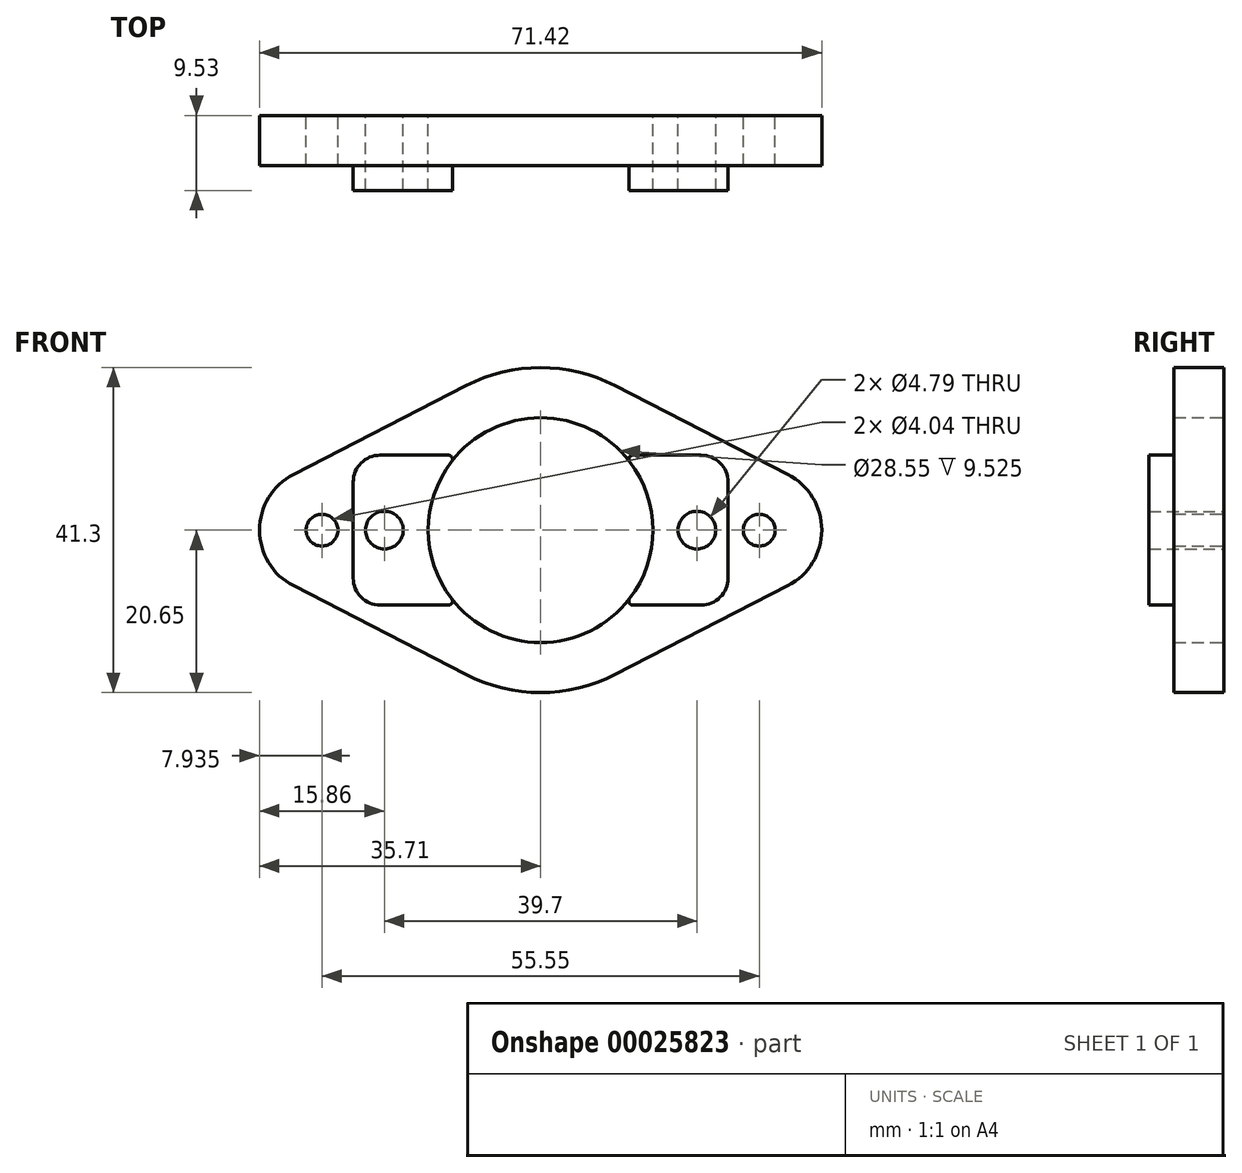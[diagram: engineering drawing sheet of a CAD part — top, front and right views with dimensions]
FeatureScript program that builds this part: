
annotation { "Feature Type Name" : "Feature", "Feature Type Description" : "" }
export const myFeature = defineFeature(function(context is Context, id is Id, definition is map)
    precondition{}
    {
        {
            var Q0;
            Q0=qCreatedBy(makeId("Front.planeOp"),FACE);
            var sketch = newSketch(context, id + "F0", { "sketchPlane" : qUnion([Q0])});
            skArc(sketch, "E0", {"start": v(-9.45, -18.36) * mm, "mid": v(0, -20.65) * mm, "end": v(9.45, -18.36) * mm});
            skArc(sketch, "E1", {"start": v(-31.4, 7.06) * mm, "mid": v(-35.71, 0) * mm, "end": v(-31.4, -7.06) * mm});
            skArc(sketch, "E2", {"start": v(31.4, -7.06) * mm, "mid": v(35.71, 0) * mm, "end": v(31.4, 7.06) * mm});
            skLineSegment(sketch, "E3", {"start": v(0, 32.22) * mm, "end": v(0, 0) * mm, "construction": true});
            skLineSegment(sketch, "E4", {"start": v(0, 0) * mm, "end": v(27.77, 0) * mm, "construction": true});
            skLineSegment(sketch, "E5", {"start": v(-31.4, 7.06) * mm, "end": v(-9.45, 18.36) * mm});
            skLineSegment(sketch, "E6", {"start": v(9.45, 18.36) * mm, "end": v(31.4, 7.06) * mm});
            skLineSegment(sketch, "E7", {"start": v(31.4, -7.06) * mm, "end": v(9.45, -18.36) * mm});
            skLineSegment(sketch, "E8", {"start": v(-31.4, -7.06) * mm, "end": v(-9.45, -18.36) * mm});
            skArc(sketch, "E9.trimOffspring", {"start": v(9.45, 18.36) * mm, "mid": v(0, 20.65) * mm, "end": v(-9.45, 18.36) * mm});
            skCircle(sketch, "E10", {"center": v(0, 0) * mm, "radius": 14.27 * mm});
            skSolve(sketch);
        }
        {
            var Q0;
            Q0=makeQuery(id+"F0.imprint","IMPRINT",FACE,{"disambiguationData":[TD([[makeQuery(id+"F0.imprint","IMPRINT",EDGE,{"derivedFrom":sQuery(id+"F0.wireOp",EDGE,"E0")}),1.0]])]});
            extrude(context, id + "F1", {"entities" : qUnion([Q0]), "depth" : 6.35 * mm});
        }
        {
            var Q0;
            Q0=makeQuery(id+"F1.opExtrude","CAP_FACE",FACE,{"disambiguationData":[OSD([sQuery(id+"F0.wireOp",EDGE,"E0"),sQuery(id+"F0.wireOp",EDGE,"E1"),sQuery(id+"F0.wireOp",EDGE,"E2"),sQuery(id+"F0.wireOp",EDGE,"E5"),sQuery(id+"F0.wireOp",EDGE,"E6"),sQuery(id+"F0.wireOp",EDGE,"E7"),sQuery(id+"F0.wireOp",EDGE,"E8"),sQuery(id+"F0.wireOp",EDGE,"E9.trimOffspring"),sQuery(id+"F0.wireOp",EDGE,"E10")])],"isStart":false});
            var sketch = newSketch(context, id + "F2", { "sketchPlane" : qUnion([Q0])});
            skLineSegment(sketch, "E11.rect.bottom", {"start": v(20.38, 9.53) * mm, "end": v(-20.38, 9.53) * mm});
            skLineSegment(sketch, "E11.rect.top", {"start": v(20.38, -9.53) * mm, "end": v(-20.38, -9.53) * mm});
            skLineSegment(sketch, "E11.rect.left", {"start": v(23.81, 6.1) * mm, "end": v(23.81, -6.1) * mm});
            skLineSegment(sketch, "E11.rect.right", {"start": v(-23.81, 6.1) * mm, "end": v(-23.81, -6.1) * mm});
            skPoint(sketch, "E11.rect.middle", {"position": v(0, 0) * mm});
            skPoint(sketch, "E12.visualSharp", {"position": v(23.81, 9.53) * mm});
            skArc(sketch, "E12.filletArc", {"start": v(23.81, 6.1) * mm, "mid": v(22.8, 8.52) * mm, "end": v(20.38, 9.53) * mm});
            skPoint(sketch, "E13.visualSharp", {"position": v(23.81, -9.53) * mm});
            skArc(sketch, "E13.filletArc", {"start": v(20.38, -9.53) * mm, "mid": v(22.8, -8.52) * mm, "end": v(23.81, -6.1) * mm});
            skPoint(sketch, "E14.visualSharp", {"position": v(-23.81, 9.53) * mm});
            skArc(sketch, "E14.filletArc", {"start": v(-20.38, 9.53) * mm, "mid": v(-22.8, 8.52) * mm, "end": v(-23.81, 6.1) * mm});
            skPoint(sketch, "E15.visualSharp", {"position": v(-23.81, -9.53) * mm});
            skArc(sketch, "E15.filletArc", {"start": v(-23.81, -6.1) * mm, "mid": v(-22.8, -8.52) * mm, "end": v(-20.38, -9.53) * mm});
            skCircle(sketch, "E16.0", {"center": v(0, 0) * mm, "radius": 14.27 * mm});
            skSolve(sketch);
        }
        {
            var Q0;
            Q0=makeQuery(id+"F2.imprint","IMPRINT",FACE,{"disambiguationData":[TD([[makeQuery(id+"F2.imprint","IMPRINT",EDGE,{"derivedFrom":sQuery(id+"F2.wireOp",EDGE,"E11.rect.right")}),1.0]])]});
            var Q1;
            Q1=makeQuery(id+"F2.imprint","IMPRINT",FACE,{"disambiguationData":[TD([[makeQuery(id+"F2.imprint","IMPRINT",EDGE,{"derivedFrom":sQuery(id+"F2.wireOp",EDGE,"E11.rect.left")}),-1.0]])]});
            extrude(context, id + "F3", {"entities" : qUnion([Q0, Q1]), "operationType" : NewBodyOperationType.ADD, "depth" : 3.17 * mm});
        }
        {
            var Q0;
            {var subQ0=sQuery(id+"F2.wireOp",EDGE,"E11.rect.bottom");var subQ1=sQuery(id+"F2.wireOp",EDGE,"E16.0");Q0=makeQuery(id+"F3.opExtrude","SWEPT_EDGE",EDGE,{"disambiguationData":[OSD([subQ0,subQ1]),TDD([makeQuery(id+"F2.imprint","INTERSECT",VERTEX,{"disambiguationData":[OD(1.0)],"derivedFrom":[subQ0,subQ1]})])]});}
            var Q1;
            {var subQ0=sQuery(id+"F2.wireOp",EDGE,"E11.rect.top");var subQ1=sQuery(id+"F2.wireOp",EDGE,"E16.0");Q1=makeQuery(id+"F3.opExtrude","SWEPT_EDGE",EDGE,{"disambiguationData":[OSD([subQ0,subQ1]),TDD([makeQuery(id+"F2.imprint","INTERSECT",VERTEX,{"disambiguationData":[OD(1.0)],"derivedFrom":[subQ0,subQ1]})])]});}
            var Q2;
            {var subQ0=sQuery(id+"F2.wireOp",EDGE,"E11.rect.bottom");var subQ1=sQuery(id+"F2.wireOp",EDGE,"E16.0");Q2=makeQuery(id+"F3.opExtrude","SWEPT_EDGE",EDGE,{"disambiguationData":[OSD([subQ0,subQ1]),TDD([makeQuery(id+"F2.imprint","INTERSECT",VERTEX,{"disambiguationData":[OD(0.0)],"derivedFrom":[subQ0,subQ1]})])]});}
            var Q3;
            {var subQ0=sQuery(id+"F2.wireOp",EDGE,"E11.rect.top");var subQ1=sQuery(id+"F2.wireOp",EDGE,"E16.0");Q3=makeQuery(id+"F3.opExtrude","SWEPT_EDGE",EDGE,{"disambiguationData":[OSD([subQ0,subQ1]),TDD([makeQuery(id+"F2.imprint","INTERSECT",VERTEX,{"disambiguationData":[OD(0.0)],"derivedFrom":[subQ0,subQ1]})])]});}
            fillet(context, id + "F4", {"entities" : qUnion([Q0, Q1, Q2, Q3]), "radius" : 0.5 * mm, "tangentPropagation" : true, "allowEdgeOverflow" : false});
        }
        {
            var Q0;
            Q0=makeQuery(id+"F1.opExtrude","CAP_FACE",FACE,{"disambiguationData":[OSD([sQuery(id+"F0.wireOp",EDGE,"E0"),sQuery(id+"F0.wireOp",EDGE,"E1"),sQuery(id+"F0.wireOp",EDGE,"E2"),sQuery(id+"F0.wireOp",EDGE,"E5"),sQuery(id+"F0.wireOp",EDGE,"E6"),sQuery(id+"F0.wireOp",EDGE,"E7"),sQuery(id+"F0.wireOp",EDGE,"E8"),sQuery(id+"F0.wireOp",EDGE,"E9.trimOffspring"),sQuery(id+"F0.wireOp",EDGE,"E10")])],"isStart":true});
            var sketch = newSketch(context, id + "F5", { "sketchPlane" : qUnion([Q0])});
            skLineSegment(sketch, "E17", {"start": v(-27.77, 0) * mm, "end": v(27.77, 0) * mm});
            skPoint(sketch, "E18", {"position": v(-19.85, 0) * mm});
            skPoint(sketch, "E19", {"position": v(19.85, 0) * mm});
            skLineSegment(sketch, "E20", {"start": v(0, 30.11) * mm, "end": v(0, 0) * mm, "construction": true});
            skSolve(sketch);
        }
        {
            var Q0;
            Q0=sQuery(id+"F5.wireOp",VERTEX,"E18");
            var Q1;
            Q1=sQuery(id+"F5.wireOp",VERTEX,"E19");
            var Q2;
            Q2=makeQuery(id+"F1.opExtrude","SWEPT_BODY",BODY,{"disambiguationData":[OSD([sQuery(id+"F0.wireOp",EDGE,"E0"),sQuery(id+"F0.wireOp",EDGE,"E1"),sQuery(id+"F0.wireOp",EDGE,"E2"),sQuery(id+"F0.wireOp",EDGE,"E5"),sQuery(id+"F0.wireOp",EDGE,"E6"),sQuery(id+"F0.wireOp",EDGE,"E7"),sQuery(id+"F0.wireOp",EDGE,"E8"),sQuery(id+"F0.wireOp",EDGE,"E9.trimOffspring"),sQuery(id+"F0.wireOp",EDGE,"E10")])]});
            hole(context, id + "F6", {"style" : HoleStyle.SIMPLE, "holeDiameter" : 4.8 * mm, "endStyle" : HoleEndStyle.THROUGH, "locations" : qUnion([Q0, Q1]), "scope" : qUnion([Q2])});
        }
        {
            var Q0;
            Q0=sQuery(id+"F5.wireOp",VERTEX,"E17.start");
            var Q1;
            Q1=sQuery(id+"F5.wireOp",VERTEX,"E17.end");
            var Q2;
            Q2=makeQuery(id+"F1.opExtrude","SWEPT_BODY",BODY,{"disambiguationData":[OSD([sQuery(id+"F0.wireOp",EDGE,"E0"),sQuery(id+"F0.wireOp",EDGE,"E1"),sQuery(id+"F0.wireOp",EDGE,"E2"),sQuery(id+"F0.wireOp",EDGE,"E5"),sQuery(id+"F0.wireOp",EDGE,"E6"),sQuery(id+"F0.wireOp",EDGE,"E7"),sQuery(id+"F0.wireOp",EDGE,"E8"),sQuery(id+"F0.wireOp",EDGE,"E9.trimOffspring"),sQuery(id+"F0.wireOp",EDGE,"E10")])]});
            hole(context, id + "F7", {"style" : HoleStyle.SIMPLE, "holeDiameter" : 4.04 * mm, "endStyle" : HoleEndStyle.THROUGH, "locations" : qUnion([Q0, Q1]), "scope" : qUnion([Q2])});
        }
    });
